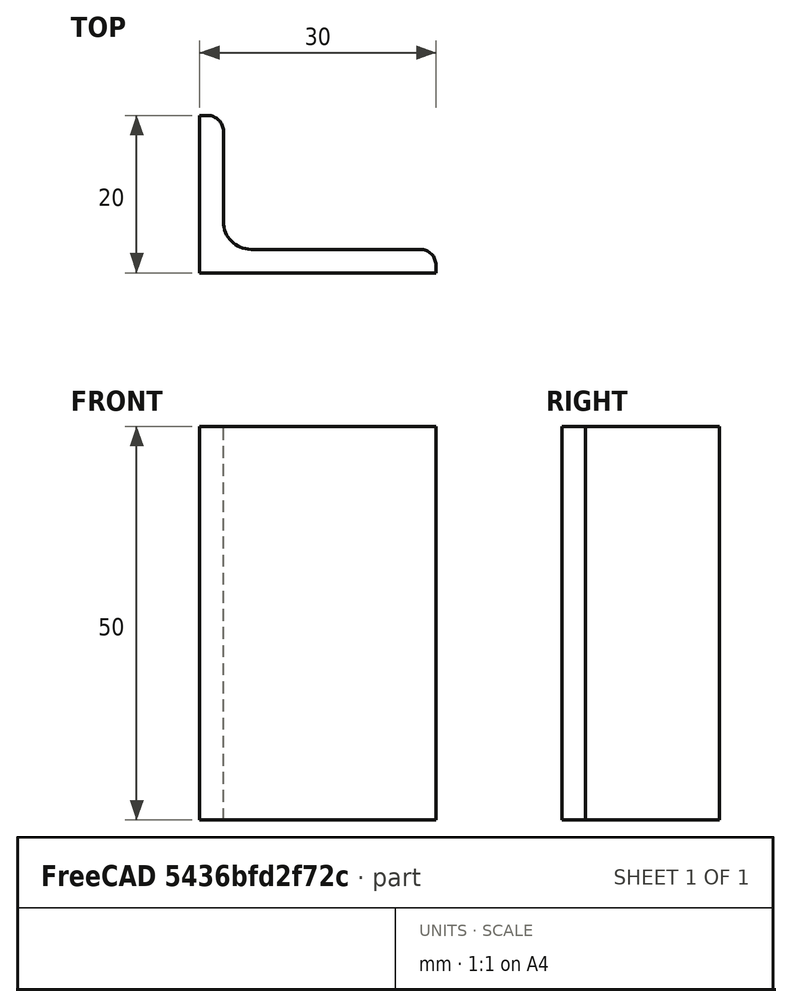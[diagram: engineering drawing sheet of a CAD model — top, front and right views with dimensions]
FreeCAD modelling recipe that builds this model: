
FCSTD DOCUMENT  (FreeCAD 0.15R4671 (Git))
Label: Angle Bar 30x20x3 EN10056 S235JR
License: All rights reserved
LicenseURL: http://en.wikipedia.org/wiki/All_rights_reserved
objects: Sketcher::SketchObject×1, Part::Extrusion×1
note: 2 computed .brp shape members not serialized (recipe doc carries the construction recipe); baked Part::Feature solids carry a one-line shape summary decoded from their .brp

FEATURE [Sketcher::SketchObject] Sketch
  sketch-geometry (9):
    g0: LineSegment StartX=0 StartY=0 StartZ=0 EndX=30 EndY=0 EndZ=0
    g1: LineSegment StartX=30 StartY=0 StartZ=0 EndX=30 EndY=1 EndZ=0
    g2: LineSegment StartX=28 StartY=3 StartZ=0 EndX=6.5 EndY=3 EndZ=0
    g3: LineSegment StartX=0 StartY=0 StartZ=0 EndX=0 EndY=20 EndZ=0
    g4: LineSegment StartX=0 StartY=20 StartZ=0 EndX=1 EndY=20 EndZ=0
    g5: LineSegment StartX=3 StartY=18 StartZ=0 EndX=3 EndY=6.5 EndZ=0
    g6: ArcOfCircle CenterX=6.5 CenterY=6.5 CenterZ=0 NormalX=0 NormalY=0 NormalZ=1 Radius=3.5 StartAngle=3.14159 EndAngle=4.71239
    g7: ArcOfCircle CenterX=1 CenterY=18 CenterZ=0 NormalX=0 NormalY=0 NormalZ=1 Radius=2 StartAngle=0 EndAngle=1.5708
    g8: ArcOfCircle CenterX=28 CenterY=1 CenterZ=0 NormalX=0 NormalY=0 NormalZ=1 Radius=2 StartAngle=0 EndAngle=1.5708
  constraints (23):
    c: Coincident(g0,g-1)
    c: Horizontal(g0)
    c: Coincident(g1,g0)
    c: Vertical(g1)
    c: Horizontal(g2)
    c: Coincident(g3,g-1)
    c: Vertical(g3)
    c: Coincident(g4,g3)
    c: Horizontal(g4)
    c: Vertical(g5)
    c: Tangent(g5,g6) = -1.5708
    c: Tangent(g2,g6) = 1.5708
    c: Tangent(g4,g7) = 1.5708
    c: Tangent(g5,g7) = 1.5708
    c: Tangent(g2,g8) = -1.5708
    c: Tangent(g1,g8) = -1.5708
    c: DistanceX(g0) = 30
    c: DistanceY(g3) = 20
    c: DistanceY(g0,g2) = 3
    c: DistanceX(g3,g5) = 3
    c: Radius(g6) = 3.5
    c: Radius(g8) = 2
    c: Radius(g7) = 2
FEATURE [Part::Extrusion] Extrude  label="Angle Bar 30x20x3 EN10056 S235JR"
  Base = -> Sketch
  Dir = (0,0,50)
  Solid = true
